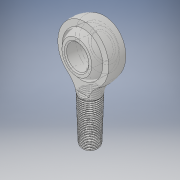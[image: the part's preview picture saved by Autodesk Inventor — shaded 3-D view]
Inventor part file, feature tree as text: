
AUTODESK INVENTOR PART (.ipt)
format: ipt  version: 2019 (Build 230136000, 136)  size: 697,856 bytes
history: native  units: in
note: dims shown in document units (in); Inventor stores cm internally (conversion verified against a paired STEP export)
features: other x1, chamfer x1
ambient origin geometry x8: Origin, YZ Plane, XZ Plane, XY Plane, X Axis, Y Axis, Z Axis, Center Point
bodies: Solid1 (feature_tree), Solid2 (feature_tree)
feature tree (2):
  other  "Cut-Extrude2"
  chamfer  "Chamfer1"  [1 undecoded]
note: 1 required parameter value undecoded (feature->parameter linkage not recoverable at this tier; creation-order binding heuristic only, values carry confidence <= 0.55)
